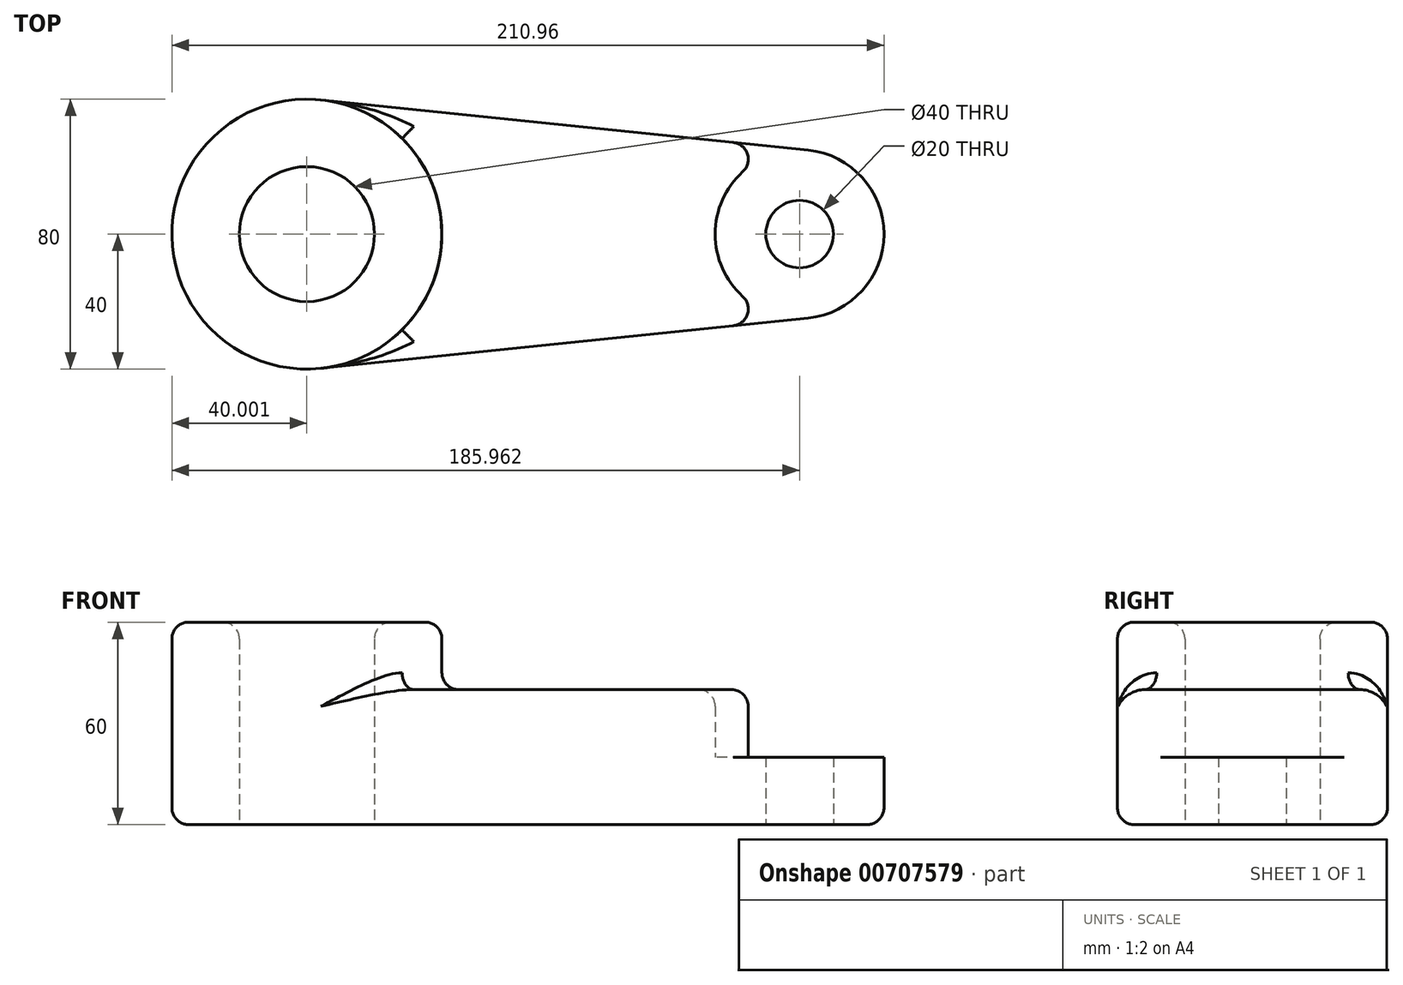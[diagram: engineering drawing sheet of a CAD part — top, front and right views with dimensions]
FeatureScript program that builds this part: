
annotation { "Feature Type Name" : "Feature", "Feature Type Description" : "" }
export const myFeature = defineFeature(function(context is Context, id is Id, definition is map)
    precondition{}
    {
        {
            var Q0;
            Q0=qCreatedBy(makeId("Top.planeOp"),FACE);
            var sketch = newSketch(context, id + "F0", { "sketchPlane" : qUnion([Q0])});
            skCircle(sketch, "E0", {"center": v(-83.1, 0) * mm, "radius": 20 * mm});
            skCircle(sketch, "E1", {"center": v(-83.1, 0) * mm, "radius": 40 * mm});
            skCircle(sketch, "E2", {"center": v(62.85, 0) * mm, "radius": 25 * mm});
            skCircle(sketch, "E3", {"center": v(62.85, 0) * mm, "radius": 10 * mm});
            skLineSegment(sketch, "E4", {"start": v(-79, 39.79) * mm, "end": v(65.42, 24.87) * mm});
            skLineSegment(sketch, "E5", {"start": v(-79, -39.79) * mm, "end": v(65.42, -24.87) * mm});
            skSolve(sketch);
        }
        {
            var Q0;
            Q0=makeQuery(id+"F0.imprint","IMPRINT",FACE,{"disambiguationData":[TD([[makeQuery(id+"F0.imprint","IMPRINT",EDGE,{"derivedFrom":sQuery(id+"F0.wireOp",EDGE,"E0")}),-1.0]])]});
            extrude(context, id + "F1", {"entities" : qUnion([Q0]), "depth" : 60 * mm, "offsetDistance" : 25 * mm});
        }
        {
            var Q0;
            {var subQ0=sQuery(id+"F0.wireOp",EDGE,"E4");Q0=makeQuery(id+"F0.imprint","IMPRINT",FACE,{"disambiguationData":[TD([[makeQuery(id+"F0.imprint","IMPRINT",EDGE,{"derivedFrom":subQ0}),-1.0]])]});}
            extrude(context, id + "F2", {"entities" : qUnion([Q0]), "operationType" : NewBodyOperationType.ADD, "depth" : 40 * mm, "offsetDistance" : 25 * mm});
        }
        {
            var Q0;
            Q0=makeQuery(id+"F0.imprint","IMPRINT",FACE,{"disambiguationData":[TD([[makeQuery(id+"F0.imprint","IMPRINT",EDGE,{"derivedFrom":sQuery(id+"F0.wireOp",EDGE,"E3")}),-1.0]])]});
            extrude(context, id + "F3", {"entities" : qUnion([Q0]), "operationType" : NewBodyOperationType.ADD, "depth" : 20 * mm, "offsetDistance" : 25 * mm});
        }
        {
            var Q0;
            Q0=makeQuery(id+"F1.opExtrude","CAP_FACE",FACE,{"disambiguationData":[OSD([sQuery(id+"F0.wireOp",EDGE,"E0"),sQuery(id+"F0.wireOp",EDGE,"E1")])],"isStart":false});
            fillet(context, id + "F4", {"entities" : qUnion([Q0]), "radius" : 5 * mm, "tangentPropagation" : true, "allowEdgeOverflow" : false});
        }
        {
            var Q0;
            Q0=makeQuery(id+"F2.opExtrude","CAP_FACE",FACE,{"disambiguationData":[OSD([sQuery(id+"F0.wireOp",EDGE,"E1"),sQuery(id+"F0.wireOp",EDGE,"E2"),sQuery(id+"F0.wireOp",EDGE,"E4"),sQuery(id+"F0.wireOp",EDGE,"E5")])],"isStart":false});
            var Q1;
            Q1=makeQuery(id+"F2.opExtrude","SWEPT_FACE",FACE,{"disambiguationData":[OSD([sQuery(id+"F0.wireOp",EDGE,"E5")])]});
            var Q2;
            Q2=makeQuery(id+"F2.opExtrude","SWEPT_FACE",FACE,{"disambiguationData":[OSD([sQuery(id+"F0.wireOp",EDGE,"E4")])]});
            fillet(context, id + "F5", {"entities" : qUnion([Q0, Q1, Q2]), "radius" : 5 * mm, "tangentPropagation" : true, "allowEdgeOverflow" : false});
        }
    });
